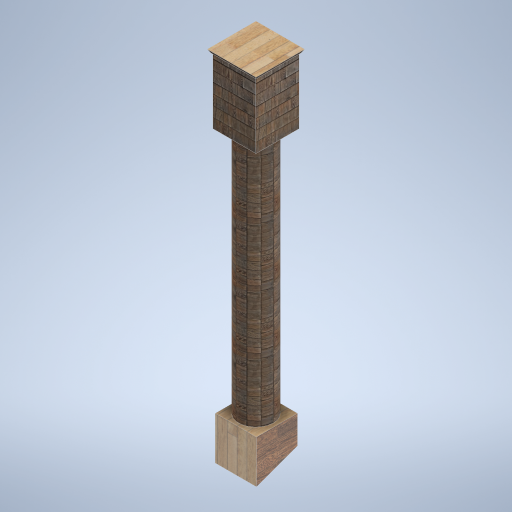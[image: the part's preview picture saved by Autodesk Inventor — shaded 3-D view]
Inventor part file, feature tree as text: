
AUTODESK INVENTOR PART (.ipt)
format: ipt  version: 2024.2 (Build 282272000, 272)  size: 351,232 bytes
history: native  units: in
note: dims shown in document units (in); Inventor stores cm internally (conversion verified against a paired STEP export)
features: sketch x5, other x3, plane x1
ambient origin geometry x8: Origin, YZ Plane, XZ Plane, XY Plane, X Axis, Y Axis, Z Axis, Center Point
bodies: Solid1 (feature_tree)
feature tree (9):
  other  "side_pillar_01.ipt"
  other  "Solid1::side_pillar_01.ipt"
  other  "TaggingFeature1"
  sketch  "Sketch1"  dims[d0=0.3937in]
  sketch  "Sketch2"
  sketch  "Sketch3"
  sketch  "Sketch4"
  sketch  "Sketch5"
  plane  "Work Plane3"
